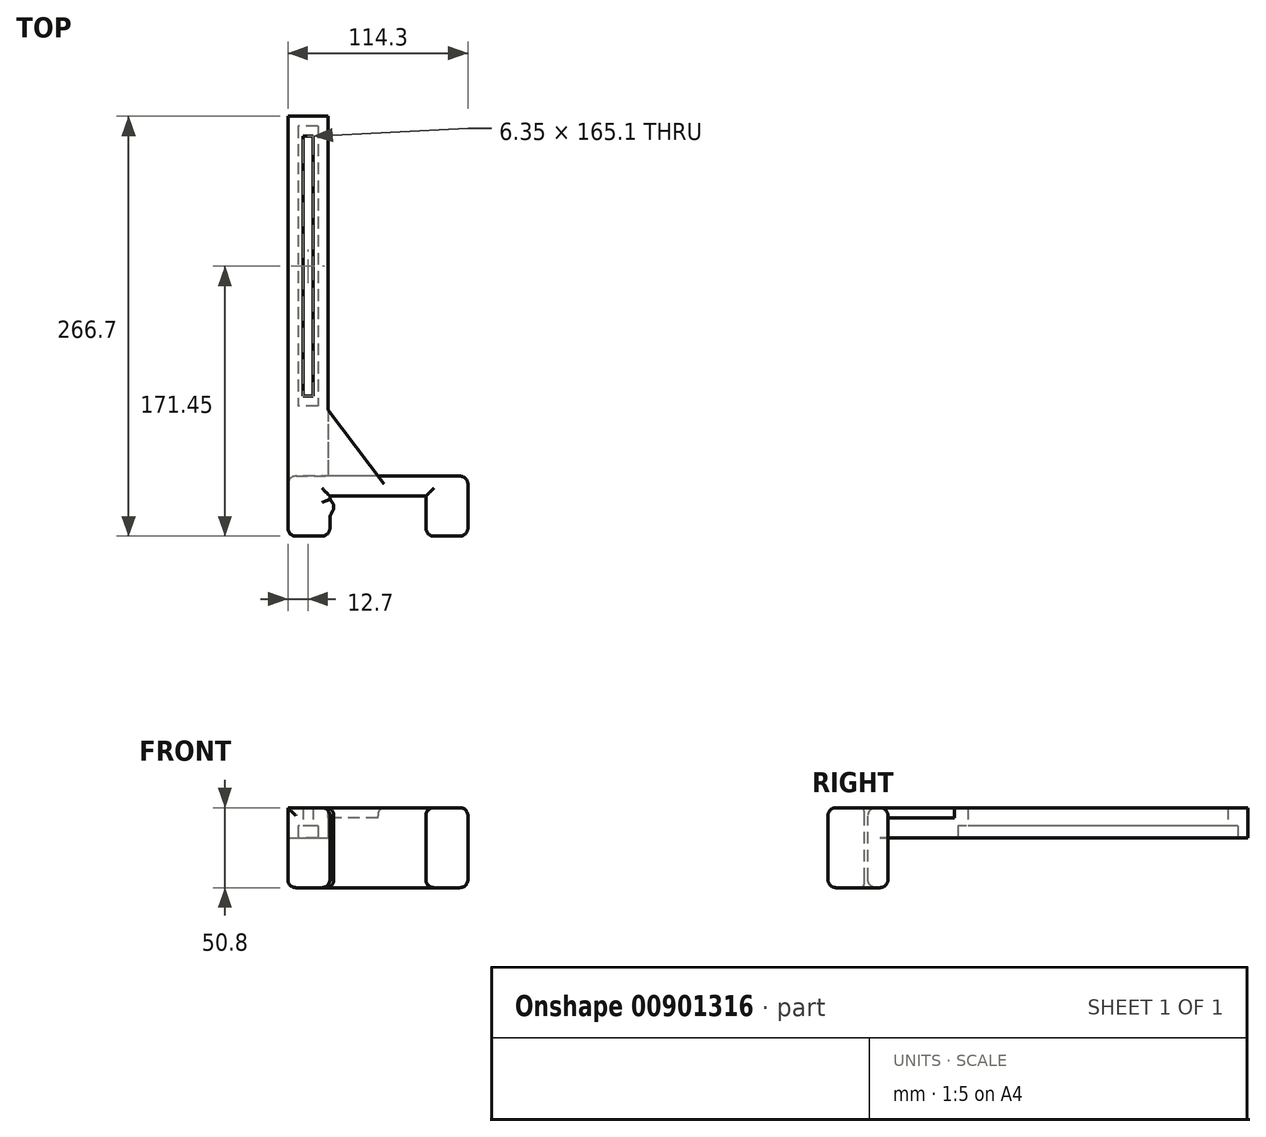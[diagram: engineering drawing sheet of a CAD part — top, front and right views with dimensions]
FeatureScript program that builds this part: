
annotation { "Feature Type Name" : "Feature", "Feature Type Description" : "" }
export const myFeature = defineFeature(function(context is Context, id is Id, definition is map)
    precondition{}
    {
        {
            var Q0;
            Q0=qCreatedBy(makeId("Top.planeOp"),FACE);
            var sketch = newSketch(context, id + "F0", { "sketchPlane" : qUnion([Q0])});
            skLineSegment(sketch, "E0.bottom", {"start": v(57.15, -19.05) * mm, "end": v(-57.15, -19.05) * mm});
            skLineSegment(sketch, "E0.top", {"start": v(57.15, 19.05) * mm, "end": v(-57.15, 19.05) * mm});
            skLineSegment(sketch, "E0.left", {"start": v(57.15, -19.05) * mm, "end": v(57.15, 19.05) * mm});
            skLineSegment(sketch, "E0.right", {"start": v(-57.15, -19.05) * mm, "end": v(-57.15, 19.05) * mm});
            skPoint(sketch, "E0.middle", {"position": v(0, 0) * mm});
            skSolve(sketch);
        }
        {
            var Q0;
            Q0=makeQuery(id+"F0.imprint","IMPRINT",FACE,{"disambiguationData":[TD([[makeQuery(id+"F0.imprint","IMPRINT",EDGE,{"derivedFrom":sQuery(id+"F0.wireOp",EDGE,"E0.bottom")}),-1.0]])]});
            var sketch = newSketch(context, id + "F1", { "sketchPlane" : qUnion([Q0])});
            skLineSegment(sketch, "E1.bottom", {"start": v(30.48, -31.75) * mm, "end": v(-30.48, -31.75) * mm});
            skLineSegment(sketch, "E1.top", {"start": v(30.48, 6.35) * mm, "end": v(-30.48, 6.35) * mm});
            skLineSegment(sketch, "E1.left", {"start": v(30.48, -31.75) * mm, "end": v(30.48, 6.35) * mm});
            skLineSegment(sketch, "E1.right", {"start": v(-30.48, -31.75) * mm, "end": v(-30.48, 6.35) * mm});
            skPoint(sketch, "E1.middle", {"position": v(0, -12.7) * mm});
            skSolve(sketch);
        }
        {
            var Q0;
            Q0=qSketchRegion(id+"F0",true);
            extrude(context, id + "F2", {"entities" : qUnion([Q0]), "depth" : 50.8 * mm, "offsetDistance" : 25.4 * mm, "symmetric" : true});
        }
        {
            var Q0;
            Q0=qSketchRegion(id+"F1",true);
            extrude(context, id + "F3", {"entities" : qUnion([Q0]), "operationType" : NewBodyOperationType.REMOVE, "oppositeDirection" : true, "depth" : 76.2 * mm, "offsetDistance" : 25.4 * mm, "symmetric" : true});
        }
        {
            var Q0;
            Q0=qCreatedBy(makeId("Top.planeOp"),FACE);
            var sketch = newSketch(context, id + "F4", { "sketchPlane" : qUnion([Q0])});
            skLineSegment(sketch, "E2", {"start": v(-30.55, 4.33) * mm, "end": v(-26.92, 0) * mm});
            skLineSegment(sketch, "E3", {"start": v(-26.92, 0) * mm, "end": v(-30.62, -6.32) * mm});
            skLineSegment(sketch, "E4", {"start": v(-30.62, -6.32) * mm, "end": v(-30.55, 4.33) * mm});
            skSolve(sketch);
        }
        {
            var Q0;
            Q0 = qSketchRegion(id + "F4", true);
            extrude(context, id + "F5", {"entities" : qUnion([Q0]), "operationType" : NewBodyOperationType.ADD, "depth" : 50.8 * mm, "offsetDistance" : 25.4 * mm, "symmetric" : true});
        }
        {
            var Q0;
            Q0=makeQuery(id+"F2.opExtrude","SWEPT_FACE",FACE,{"disambiguationData":[OSD([sQuery(id+"F0.wireOp",EDGE,"E0.top")])]});
            var sketch = newSketch(context, id + "F6", { "sketchPlane" : qUnion([Q0])});
            skLineSegment(sketch, "E5.bottom", {"start": v(57.15, 25.4) * mm, "end": v(31.75, 25.4) * mm});
            skLineSegment(sketch, "E5.top", {"start": v(57.15, 6.35) * mm, "end": v(31.75, 6.35) * mm});
            skLineSegment(sketch, "E5.left", {"start": v(57.15, 25.4) * mm, "end": v(57.15, 6.35) * mm});
            skLineSegment(sketch, "E5.right", {"start": v(31.75, 25.4) * mm, "end": v(31.75, 6.35) * mm});
            skSolve(sketch);
        }
        {
            var Q0;
            Q0=makeQuery(id+"F6.imprint","IMPRINT",FACE,{"disambiguationData":[TD([[makeQuery(id+"F6.imprint","IMPRINT",EDGE,{"derivedFrom":sQuery(id+"F6.wireOp",EDGE,"E5.bottom")}),-1.0]])]});
            extrude(context, id + "F7", {"entities" : qUnion([Q0]), "operationType" : NewBodyOperationType.ADD, "depth" : 228.6 * mm, "offsetDistance" : 25.4 * mm});
        }
        {
            var Q0;
            Q0=makeQuery(id+"F7.opExtrude","SWEPT_FACE",FACE,{"disambiguationData":[OSD([sQuery(id+"F6.wireOp",EDGE,"E5.top")])]});
            var sketch = newSketch(context, id + "F8", { "sketchPlane" : qUnion([Q0])});
            skLineSegment(sketch, "E6.bottom", {"start": v(-38.1, -241.3) * mm, "end": v(-50.8, -241.3) * mm});
            skLineSegment(sketch, "E6.top", {"start": v(-38.1, -63.5) * mm, "end": v(-50.8, -63.5) * mm});
            skLineSegment(sketch, "E6.left", {"start": v(-38.1, -241.3) * mm, "end": v(-38.1, -63.5) * mm});
            skLineSegment(sketch, "E6.right", {"start": v(-50.8, -241.3) * mm, "end": v(-50.8, -63.5) * mm});
            skSolve(sketch);
        }
        {
            var Q0;
            Q0=makeQuery(id+"F8.imprint","IMPRINT",FACE,{"disambiguationData":[TD([[makeQuery(id+"F8.imprint","IMPRINT",EDGE,{"derivedFrom":sQuery(id+"F8.wireOp",EDGE,"E6.bottom")}),-1.0]])]});
            extrude(context, id + "F9", {"entities" : qUnion([Q0]), "operationType" : NewBodyOperationType.REMOVE, "oppositeDirection" : true, "depth" : 7.62 * mm, "offsetDistance" : 25.4 * mm});
        }
        {
            var Q0;
            Q0=makeQuery(id+"F9.boolean.opBoolean","COPY",FACE,{"derivedFrom":makeQuery(id+"F9.opExtrude","CAP_FACE",FACE,{"disambiguationData":[OSD([sQuery(id+"F8.wireOp",EDGE,"E6.bottom"),sQuery(id+"F8.wireOp",EDGE,"E6.top"),sQuery(id+"F8.wireOp",EDGE,"E6.left"),sQuery(id+"F8.wireOp",EDGE,"E6.right")])],"isStart":false})});
            var sketch = newSketch(context, id + "F10", { "sketchPlane" : qUnion([Q0])});
            skLineSegment(sketch, "E7.bottom", {"start": v(-41.27, -234.95) * mm, "end": v(-47.62, -234.95) * mm});
            skLineSegment(sketch, "E7.top", {"start": v(-41.28, -69.85) * mm, "end": v(-47.63, -69.85) * mm});
            skLineSegment(sketch, "E7.left", {"start": v(-41.27, -234.95) * mm, "end": v(-41.28, -69.85) * mm});
            skLineSegment(sketch, "E7.right", {"start": v(-47.62, -234.95) * mm, "end": v(-47.63, -69.85) * mm});
            skSolve(sketch);
        }
        {
            var Q0;
            Q0=makeQuery(id+"F10.imprint","IMPRINT",FACE,{"disambiguationData":[TD([[makeQuery(id+"F10.imprint","IMPRINT",EDGE,{"derivedFrom":sQuery(id+"F10.wireOp",EDGE,"E7.bottom")}),-1.0]])]});
            extrude(context, id + "F11", {"entities" : qUnion([Q0]), "operationType" : NewBodyOperationType.REMOVE, "endBound" : BoundingType.THROUGH_ALL, "oppositeDirection" : true, "depth" : 25.4 * mm, "offsetDistance" : 25.4 * mm});
        }
        {
            var Q0;
            Q0=makeQuery(id+"F7.boolean.opBoolean","MERGE",FACE,{"derivedFrom":[makeQuery(id+"F5.boolean.opBoolean","MERGE",FACE,{"derivedFrom":[makeQuery(id+"F2.opExtrude","CAP_FACE",FACE,{"disambiguationData":[OSD([sQuery(id+"F0.wireOp",EDGE,"E0.bottom"),sQuery(id+"F0.wireOp",EDGE,"E0.top"),sQuery(id+"F0.wireOp",EDGE,"E0.left"),sQuery(id+"F0.wireOp",EDGE,"E0.right")])],"isStart":false}),makeQuery(id+"F5.opExtrude","CAP_FACE",FACE,{"disambiguationData":[OSD([sQuery(id+"F4.wireOp",EDGE,"qLtYSuud-ph1T-BqKs-XRN0-yXMVc8EafQEn"),sQuery(id+"F4.wireOp",EDGE,"RoyMUM6X-8VMM-Sl8T-uHXF-BxYS1tLdU7Pl"),sQuery(id+"F4.wireOp",EDGE,"0XjcN8wQ-co3J-NBqf-NEGk-mq43l9WgmgQX")])],"isStart":false})]}),makeQuery(id+"F7.opExtrude","SWEPT_FACE",FACE,{"disambiguationData":[OSD([sQuery(id+"F6.wireOp",EDGE,"E5.bottom")])]})]});
            var sketch = newSketch(context, id + "F12", { "sketchPlane" : qUnion([Q0])});
            skLineSegment(sketch, "E8", {"start": v(-31.75, 61.16) * mm, "end": v(0, 19.05) * mm});
            skLineSegment(sketch, "E9", {"start": v(0, 19.05) * mm, "end": v(-31.75, 19.05) * mm});
            skLineSegment(sketch, "E10", {"start": v(-31.75, 19.05) * mm, "end": v(-31.75, 61.16) * mm});
            skSolve(sketch);
        }
        {
            var Q0;
            Q0=makeQuery(id+"F12.imprint","IMPRINT",FACE,{"disambiguationData":[TD([[makeQuery(id+"F12.imprint","IMPRINT",EDGE,{"derivedFrom":sQuery(id+"F12.wireOp",EDGE,"E8")}),-1.0]])]});
            extrude(context, id + "F13", {"entities" : qUnion([Q0]), "operationType" : NewBodyOperationType.ADD, "oppositeDirection" : true, "depth" : 6.35 * mm, "offsetDistance" : 25.4 * mm});
        }
        {
            var Q0;
            Q0=makeQuery(id+"F2.opExtrude","CAP_EDGE",EDGE,{"disambiguationData":[OSD([sQuery(id+"F0.wireOp",EDGE,"E0.top")])],"isStart":false});
            var Q1;
            Q1=makeQuery(id+"F2.opExtrude","SWEPT_EDGE",EDGE,{"disambiguationData":[OSD([sQuery(id+"F0.wireOp",EDGE,"E0.top"),sQuery(id+"F0.wireOp",EDGE,"E0.left")])]});
            var Q2;
            Q2=makeQuery(id+"F2.opExtrude","CAP_EDGE",EDGE,{"disambiguationData":[OSD([sQuery(id+"F0.wireOp",EDGE,"E0.top")])],"isStart":true});
            var Q3;
            Q3=makeQuery(id+"F2.opExtrude","SWEPT_EDGE",EDGE,{"disambiguationData":[OSD([sQuery(id+"F0.wireOp",EDGE,"E0.top"),sQuery(id+"F0.wireOp",EDGE,"E0.right")])]});
            var Q4;
            Q4=makeQuery(id+"F2.opExtrude","CAP_EDGE",EDGE,{"disambiguationData":[OSD([sQuery(id+"F0.wireOp",EDGE,"E0.right")])],"isStart":true});
            var Q5;
            {var subQ0=makeQuery(id+"F3.opExtrude","SWEPT_FACE",FACE,{"disambiguationData":[OSD([sQuery(id+"F1.wireOp",EDGE,"E1.right")])]});var subQ2=sQuery(id+"F0.wireOp",EDGE,"E0.bottom");var subQ3=makeQuery(id+"F2.opExtrude","CAP_FACE",FACE,{"disambiguationData":[OSD([subQ2,sQuery(id+"F0.wireOp",EDGE,"E0.top"),sQuery(id+"F0.wireOp",EDGE,"E0.left"),sQuery(id+"F0.wireOp",EDGE,"E0.right")])],"isStart":true});Q5=makeQuery(id+"F5.boolean.opBoolean","SPLIT",EDGE,{"disambiguationData":[TD([makeQuery(id+"F2.opExtrude","SWEPT_FACE",FACE,{"disambiguationData":[OSD([subQ2])]})])],"derivedFrom":makeQuery(id+"F3.boolean.opBoolean","INTERSECT",EDGE,{"derivedFrom":[subQ3,subQ0]})});}
            var Q6;
            Q6=makeQuery(id+"F2.opExtrude","SWEPT_EDGE",EDGE,{"disambiguationData":[OSD([sQuery(id+"F0.wireOp",EDGE,"E0.bottom"),sQuery(id+"F0.wireOp",EDGE,"E0.right")])]});
            var Q7;
            Q7=makeQuery(id+"F2.opExtrude","CAP_EDGE",EDGE,{"disambiguationData":[OSD([sQuery(id+"F0.wireOp",EDGE,"E0.left")])],"isStart":false});
            var Q8;
            Q8=makeQuery(id+"F2.opExtrude","CAP_EDGE",EDGE,{"disambiguationData":[OSD([sQuery(id+"F0.wireOp",EDGE,"E0.left")])],"isStart":true});
            var Q9;
            Q9=makeQuery(id+"F3.boolean.opBoolean","INTERSECT",EDGE,{"derivedFrom":[makeQuery(id+"F2.opExtrude","CAP_FACE",FACE,{"disambiguationData":[OSD([sQuery(id+"F0.wireOp",EDGE,"E0.bottom"),sQuery(id+"F0.wireOp",EDGE,"E0.top"),sQuery(id+"F0.wireOp",EDGE,"E0.left"),sQuery(id+"F0.wireOp",EDGE,"E0.right")])],"isStart":false}),makeQuery(id+"F3.opExtrude","SWEPT_FACE",FACE,{"disambiguationData":[OSD([sQuery(id+"F1.wireOp",EDGE,"E1.left")])]})]});
            var Q10;
            Q10=makeQuery(id+"F2.opExtrude","SWEPT_EDGE",EDGE,{"disambiguationData":[OSD([sQuery(id+"F0.wireOp",EDGE,"E0.bottom"),sQuery(id+"F0.wireOp",EDGE,"E0.left")])]});
            var Q11;
            {var subQ0=sQuery(id+"F0.wireOp",EDGE,"E0.bottom");var subQ1=sQuery(id+"F0.wireOp",EDGE,"E0.left");Q11=makeQuery(id+"F3.boolean.opBoolean","SPLIT",EDGE,{"disambiguationData":[TD([makeQuery(id+"F2.opExtrude","SWEPT_FACE",FACE,{"disambiguationData":[OSD([subQ1])]})])],"derivedFrom":makeQuery(id+"F2.opExtrude","CAP_EDGE",EDGE,{"disambiguationData":[OSD([subQ0])],"isStart":false})});}
            var Q12;
            Q12=makeQuery(id+"F3.boolean.opBoolean","INTERSECT",EDGE,{"derivedFrom":[makeQuery(id+"F2.opExtrude","SWEPT_FACE",FACE,{"disambiguationData":[OSD([sQuery(id+"F0.wireOp",EDGE,"E0.bottom")])]}),makeQuery(id+"F3.opExtrude","SWEPT_FACE",FACE,{"disambiguationData":[OSD([sQuery(id+"F1.wireOp",EDGE,"E1.left")])]})]});
            var Q13;
            {var subQ0=sQuery(id+"F0.wireOp",EDGE,"E0.bottom");var subQ1=sQuery(id+"F0.wireOp",EDGE,"E0.left");Q13=makeQuery(id+"F3.boolean.opBoolean","SPLIT",EDGE,{"disambiguationData":[TD([makeQuery(id+"F2.opExtrude","SWEPT_FACE",FACE,{"disambiguationData":[OSD([subQ1])]})])],"derivedFrom":makeQuery(id+"F2.opExtrude","CAP_EDGE",EDGE,{"disambiguationData":[OSD([subQ0])],"isStart":true})});}
            var Q14;
            Q14=makeQuery(id+"F3.boolean.opBoolean","INTERSECT",EDGE,{"derivedFrom":[makeQuery(id+"F2.opExtrude","CAP_FACE",FACE,{"disambiguationData":[OSD([sQuery(id+"F0.wireOp",EDGE,"E0.bottom"),sQuery(id+"F0.wireOp",EDGE,"E0.top"),sQuery(id+"F0.wireOp",EDGE,"E0.left"),sQuery(id+"F0.wireOp",EDGE,"E0.right")])],"isStart":false}),makeQuery(id+"F3.opExtrude","SWEPT_FACE",FACE,{"disambiguationData":[OSD([sQuery(id+"F1.wireOp",EDGE,"E1.top")])]})]});
            var Q15;
            {var subQ1=makeQuery(id+"F3.opExtrude","SWEPT_FACE",FACE,{"disambiguationData":[OSD([sQuery(id+"F1.wireOp",EDGE,"E1.right")])]});var subQ2=makeQuery(id+"F2.opExtrude","CAP_FACE",FACE,{"disambiguationData":[OSD([sQuery(id+"F0.wireOp",EDGE,"E0.bottom"),sQuery(id+"F0.wireOp",EDGE,"E0.top"),sQuery(id+"F0.wireOp",EDGE,"E0.left"),sQuery(id+"F0.wireOp",EDGE,"E0.right")])],"isStart":false});Q15=makeQuery(id+"F5.boolean.opBoolean","SPLIT",EDGE,{"disambiguationData":[TD([makeQuery(id+"F3.boolean.opBoolean","COPY",FACE,{"derivedFrom":makeQuery(id+"F3.opExtrude","SWEPT_FACE",FACE,{"disambiguationData":[OSD([sQuery(id+"F1.wireOp",EDGE,"E1.top")])]})})])],"derivedFrom":makeQuery(id+"F3.boolean.opBoolean","INTERSECT",EDGE,{"derivedFrom":[subQ2,subQ1]})});}
            var Q16;
            {var subQ0=makeQuery(id+"F3.opExtrude","SWEPT_FACE",FACE,{"disambiguationData":[OSD([sQuery(id+"F1.wireOp",EDGE,"E1.right")])]});var subQ2=sQuery(id+"F0.wireOp",EDGE,"E0.bottom");var subQ3=makeQuery(id+"F2.opExtrude","CAP_FACE",FACE,{"disambiguationData":[OSD([subQ2,sQuery(id+"F0.wireOp",EDGE,"E0.top"),sQuery(id+"F0.wireOp",EDGE,"E0.left"),sQuery(id+"F0.wireOp",EDGE,"E0.right")])],"isStart":false});Q16=makeQuery(id+"F5.boolean.opBoolean","SPLIT",EDGE,{"disambiguationData":[TD([makeQuery(id+"F2.opExtrude","SWEPT_FACE",FACE,{"disambiguationData":[OSD([subQ2])]})])],"derivedFrom":makeQuery(id+"F3.boolean.opBoolean","INTERSECT",EDGE,{"derivedFrom":[subQ3,subQ0]})});}
            var Q17;
            Q17=makeQuery(id+"F3.boolean.opBoolean","INTERSECT",EDGE,{"derivedFrom":[makeQuery(id+"F2.opExtrude","SWEPT_FACE",FACE,{"disambiguationData":[OSD([sQuery(id+"F0.wireOp",EDGE,"E0.bottom")])]}),makeQuery(id+"F3.opExtrude","SWEPT_FACE",FACE,{"disambiguationData":[OSD([sQuery(id+"F1.wireOp",EDGE,"E1.right")])]})]});
            var Q18;
            {var subQ0=sQuery(id+"F0.wireOp",EDGE,"E0.bottom");var subQ1=sQuery(id+"F0.wireOp",EDGE,"E0.right");Q18=makeQuery(id+"F3.boolean.opBoolean","SPLIT",EDGE,{"disambiguationData":[TD([makeQuery(id+"F2.opExtrude","SWEPT_FACE",FACE,{"disambiguationData":[OSD([subQ1])]})])],"derivedFrom":makeQuery(id+"F2.opExtrude","CAP_EDGE",EDGE,{"disambiguationData":[OSD([subQ0])],"isStart":true})});}
            var Q19;
            {var subQ0=sQuery(id+"F0.wireOp",EDGE,"E0.right");var subQ3=sQuery(id+"F0.wireOp",EDGE,"E0.bottom");Q19=makeQuery(id+"F3.boolean.opBoolean","SPLIT",FACE,{"disambiguationData":[TD([makeQuery(id+"F2.opExtrude","SWEPT_FACE",FACE,{"disambiguationData":[OSD([subQ0])]})])],"derivedFrom":makeQuery(id+"F2.opExtrude","SWEPT_FACE",FACE,{"disambiguationData":[OSD([subQ3])]})});}
            var Q20;
            Q20=makeQuery(id+"F3.boolean.opBoolean","INTERSECT",EDGE,{"derivedFrom":[makeQuery(id+"F2.opExtrude","CAP_FACE",FACE,{"disambiguationData":[OSD([sQuery(id+"F0.wireOp",EDGE,"E0.bottom"),sQuery(id+"F0.wireOp",EDGE,"E0.top"),sQuery(id+"F0.wireOp",EDGE,"E0.left"),sQuery(id+"F0.wireOp",EDGE,"E0.right")])],"isStart":true}),makeQuery(id+"F3.opExtrude","SWEPT_FACE",FACE,{"disambiguationData":[OSD([sQuery(id+"F1.wireOp",EDGE,"E1.left")])]})]});
            var Q21;
            Q21=makeQuery(id+"F5.opExtrude","SWEPT_EDGE",EDGE,{"disambiguationData":[OSD([sQuery(id+"F4.wireOp",EDGE,"E2"),sQuery(id+"F4.wireOp",EDGE,"E3")])]});
            var Q22;
            Q22=makeQuery(id+"F5.opExtrude","CAP_EDGE",EDGE,{"disambiguationData":[OSD([sQuery(id+"F4.wireOp",EDGE,"E2")])],"isStart":false});
            var Q23;
            Q23=makeQuery(id+"F5.boolean.opBoolean","INTERSECT",EDGE,{"derivedFrom":[makeQuery(id+"F3.boolean.opBoolean","COPY",FACE,{"derivedFrom":makeQuery(id+"F3.opExtrude","SWEPT_FACE",FACE,{"disambiguationData":[OSD([sQuery(id+"F1.wireOp",EDGE,"E1.right")])]})}),makeQuery(id+"F5.opExtrude","SWEPT_FACE",FACE,{"disambiguationData":[OSD([sQuery(id+"F4.wireOp",EDGE,"E3")])]})]});
            var Q24;
            Q24=makeQuery(id+"F5.opExtrude","CAP_EDGE",EDGE,{"disambiguationData":[OSD([sQuery(id+"F4.wireOp",EDGE,"E3")])],"isStart":false});
            var Q25;
            Q25=makeQuery(id+"F3.boolean.opBoolean","INTERSECT",EDGE,{"derivedFrom":[makeQuery(id+"F2.opExtrude","CAP_FACE",FACE,{"disambiguationData":[OSD([sQuery(id+"F0.wireOp",EDGE,"E0.bottom"),sQuery(id+"F0.wireOp",EDGE,"E0.top"),sQuery(id+"F0.wireOp",EDGE,"E0.left"),sQuery(id+"F0.wireOp",EDGE,"E0.right")])],"isStart":true}),makeQuery(id+"F3.opExtrude","SWEPT_FACE",FACE,{"disambiguationData":[OSD([sQuery(id+"F1.wireOp",EDGE,"E1.top")])]})]});
            var Q26;
            Q26=makeQuery(id+"F5.opExtrude","CAP_EDGE",EDGE,{"disambiguationData":[OSD([sQuery(id+"F4.wireOp",EDGE,"E3")])],"isStart":true});
            var Q27;
            Q27=makeQuery(id+"F5.opExtrude","CAP_EDGE",EDGE,{"disambiguationData":[OSD([sQuery(id+"F4.wireOp",EDGE,"E2")])],"isStart":true});
            var Q28;
            Q28=makeQuery(id+"F5.boolean.opBoolean","MERGE",FACE,{"derivedFrom":[makeQuery(id+"F2.opExtrude","CAP_FACE",FACE,{"disambiguationData":[OSD([sQuery(id+"F0.wireOp",EDGE,"E0.bottom"),sQuery(id+"F0.wireOp",EDGE,"E0.top"),sQuery(id+"F0.wireOp",EDGE,"E0.left"),sQuery(id+"F0.wireOp",EDGE,"E0.right")])],"isStart":true}),makeQuery(id+"F5.opExtrude","CAP_FACE",FACE,{"disambiguationData":[OSD([sQuery(id+"F4.wireOp",EDGE,"E2"),sQuery(id+"F4.wireOp",EDGE,"E3"),sQuery(id+"F4.wireOp",EDGE,"E4")])],"isStart":true})]});
            var Q29;
            {var subQ1=makeQuery(id+"F3.opExtrude","SWEPT_FACE",FACE,{"disambiguationData":[OSD([sQuery(id+"F1.wireOp",EDGE,"E1.right")])]});var subQ2=makeQuery(id+"F2.opExtrude","CAP_FACE",FACE,{"disambiguationData":[OSD([sQuery(id+"F0.wireOp",EDGE,"E0.bottom"),sQuery(id+"F0.wireOp",EDGE,"E0.top"),sQuery(id+"F0.wireOp",EDGE,"E0.left"),sQuery(id+"F0.wireOp",EDGE,"E0.right")])],"isStart":true});Q29=makeQuery(id+"F5.boolean.opBoolean","SPLIT",EDGE,{"disambiguationData":[TD([makeQuery(id+"F3.boolean.opBoolean","COPY",FACE,{"derivedFrom":makeQuery(id+"F3.opExtrude","SWEPT_FACE",FACE,{"disambiguationData":[OSD([sQuery(id+"F1.wireOp",EDGE,"E1.top")])]})})])],"derivedFrom":makeQuery(id+"F3.boolean.opBoolean","INTERSECT",EDGE,{"derivedFrom":[subQ2,subQ1]})});}
            fillet(context, id + "F14", {"entities" : qUnion([Q0, Q1, Q2, Q3, Q4, Q5, Q6, Q7, Q8, Q9, Q10, Q11, Q12, Q13, Q14, Q15, Q16, Q17, Q18, Q19, Q20, Q21, Q22, Q23, Q24, Q25, Q26, Q27, Q28, Q29]), "radius" : 5.08 * mm, "tangentPropagation" : true, "allowEdgeOverflow" : false});
        }
    });
